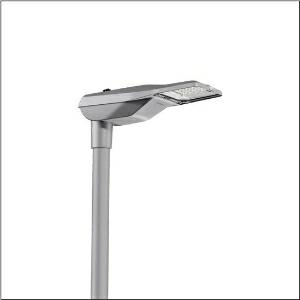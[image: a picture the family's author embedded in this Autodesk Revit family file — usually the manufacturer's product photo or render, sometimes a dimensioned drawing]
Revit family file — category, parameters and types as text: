
# Revit family: streetlight_sl_21_micro___p0_5a_5xe1v33s08db_1111
name_source: partatom
category: Lighting Fixtures
units: mm (PartAtom-declared; Revit-internal decimal feet)

## family parameters
Cut with Voids When Loaded = No
Host = Face
Light Source = No
Part Type = Normal
Room Calculation Point = No
Round Connector Dimension = Use Diameter
Shared = No

## types (1)
- --- (1 x LED, 4940 lm, 39.1 W, 3000K)
    Apparent Load = 39 VA
    CIE Flux Codes = 37 73 96 100 100
    Color Rendering = 70
    Color Temperature = 3000K
    Default Elevation = 1800 mm
    Description = Streetlight SL 21 micro, mast luminaire, primary light control with lens, of PMMA, primary optical cover: cover, of toughened safety glass, transparent, light distribution: P0.5a, light emission: direct distribution, primary light characteristic: asymmetric, installation type: post-top, side-entry, LED, High Power LED, rated luminous flux: 4.940lm, luminous efficacy: 126lm/W, light colour: 730, colour temperature: 3000K, control gear: D4i, control: pre-setting: logarithmic dimming characteristic, flexible luminous flux parameterisation, time-dependent luminous flux control, constant luminous flux control, overheat protection, mains connection: 220..240V, AC, 50/60Hz, start of lifetime: 39W, end of service life: 41W, reduction: 18W, luminaire housing, of diecast aluminium, powder-coated, SITECO metallic grey (DB 702S), corrosivity category C5 high according to DIN EN ISO 12944, multi-level sealing system, sealing non-destructively replaceable, inclination adjustable: 0°, 5°, 10°, 15°, please order mast flange separately, length: 528mm, width: 235mm, height: 110mm, mast flange for spigot size: 42mm (side-entry): 5XC10008XM4, 60/48mm (side-entry/post-top): 5XC10108XM2, 76/60mm (side-entry/post-top): 5XC10108XM1, Smart Interface above, protection rating (complete): IP66, insulation class (complete): insulation class II (safety insulation), certification: CE, ENEC, ENEC+, VDE, impact resistance: IK10, permissible operating ambient temperature for outdoor applications: -40..+50°C, standard-compliant lighting for roads and squares, packaging unit: 1 piece

Light Distribution: P0.5a
    Height = 110 mm
    Lamp = 1 x LED
    Lamp Light Flux = 4940 lm
    Lamp Power = 39.1 W
    Lamp count = 1
    Length = 528 mm
    Luminous efficacy = 126 lm/W
    Manufacturer = Siteco
    ModVariant = No
    Model = 5XE1V33S08DB
    Number of Poles = 1
    OnlyDefault = Yes
    Power Factor = 1
    Product Name = Streetlight SL 21 micro | P0.5a
    Product group = mast luminaire | pylon top
    ProductGroupID = 6100
    Protection Class = Protection class II
    Protection Degree = IP 66
    RLX_Detail_Level = 1
    RLX_Emergency_Light_Flux = 0 lm
    RLX_Emergency_Type = 0
    RLX_Emergency_Type_DB = No
    RlxData = <blob elided: 97741 chars, md5=db6eb9bc>
    Socket = socket
    Standby Power = 0 W
    System Light Flux = 4940 lm
    System Power = 39 W
    Type Comments = factory setting: luminous flux: 100 % | dim-lin: 254 | 765 mA
    Type Image = l_1277292.jpg
    URL = http://relux.com
    VarID = @adj_077845
    Voltage = 0 V
    Weight = 0.00 kg
    Width = 235 mm

## geometry (parser evidence)
native form markers: Blend x4, Sweep x9
no freeform markers — native parametric forms only
